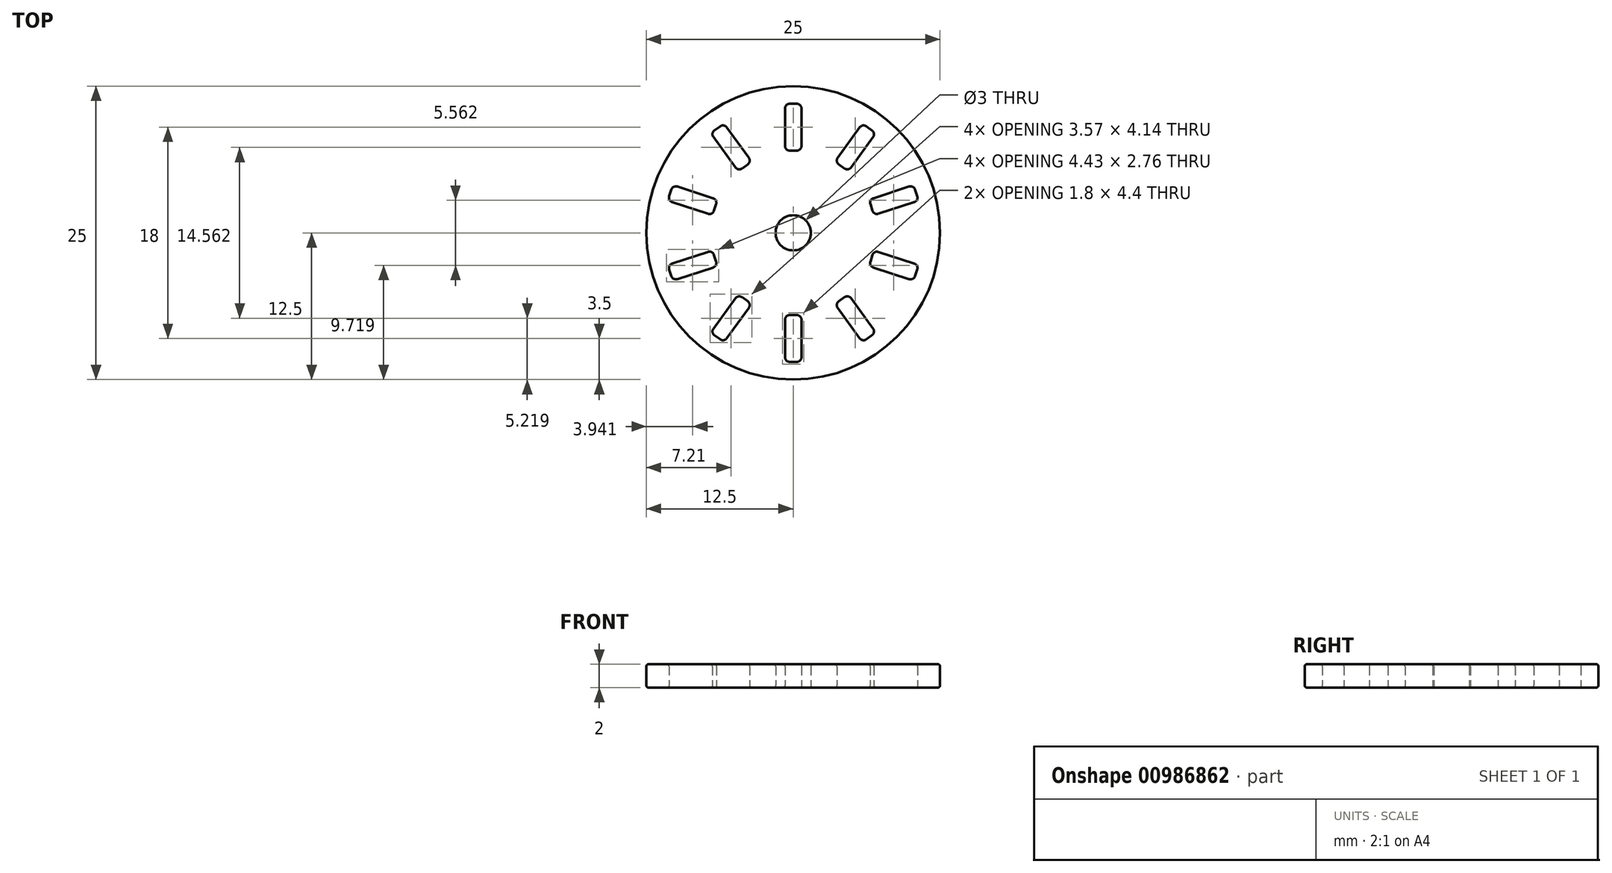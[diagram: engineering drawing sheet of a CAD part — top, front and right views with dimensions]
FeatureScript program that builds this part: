
annotation { "Feature Type Name" : "Feature", "Feature Type Description" : "" }
export const myFeature = defineFeature(function(context is Context, id is Id, definition is map)
    precondition{}
    {
        {
            var Q0;
            Q0=qCreatedBy(makeId("Top.planeOp"),FACE);
            var sketch = newSketch(context, id + "F0", { "sketchPlane" : qUnion([Q0])});
            skCircle(sketch, "E0", {"center": v(0, 0) * mm, "radius": 12.5 * mm});
            skCircle(sketch, "E1", {"center": v(0, 0) * mm, "radius": 9 * mm, "construction": true});
            skLineSegment(sketch, "E2.bottom", {"start": v(0.3, 11) * mm, "end": v(-0.3, 11) * mm});
            skLineSegment(sketch, "E2.top", {"start": v(0.3, 7) * mm, "end": v(-0.3, 7) * mm});
            skLineSegment(sketch, "E2.left", {"start": v(0.7, 10.6) * mm, "end": v(0.7, 7.4) * mm});
            skLineSegment(sketch, "E2.right", {"start": v(-0.7, 10.6) * mm, "end": v(-0.7, 7.4) * mm});
            skPoint(sketch, "E2.middle", {"position": v(0, 9) * mm});
            skPoint(sketch, "E3.visualSharp", {"position": v(-0.7, 11) * mm});
            skArc(sketch, "E3.filletArc", {"start": v(-0.3, 11) * mm, "mid": v(-0.58, 10.88) * mm, "end": v(-0.7, 10.6) * mm});
            skPoint(sketch, "E4.visualSharp", {"position": v(0.7, 11) * mm});
            skArc(sketch, "E4.filletArc", {"start": v(0.7, 10.6) * mm, "mid": v(0.58, 10.88) * mm, "end": v(0.3, 11) * mm});
            skPoint(sketch, "E5.visualSharp", {"position": v(0.7, 7) * mm});
            skArc(sketch, "E5.filletArc", {"start": v(0.3, 7) * mm, "mid": v(0.58, 7.12) * mm, "end": v(0.7, 7.4) * mm});
            skPoint(sketch, "E6.visualSharp", {"position": v(-0.7, 7) * mm});
            skArc(sketch, "E6.filletArc", {"start": v(-0.7, 7.4) * mm, "mid": v(-0.58, 7.12) * mm, "end": v(-0.3, 7) * mm});
            skLineSegment(sketch, "E7.1.0", {"start": v(-5.66, 8.99) * mm, "end": v(-3.78, 6.4) * mm});
            skPoint(sketch, "E7.1.1", {"position": v(-3.55, 6.07) * mm});
            skPoint(sketch, "E7.1.2", {"position": v(-5.3, 7.28) * mm});
            skPoint(sketch, "E7.1.3", {"position": v(-4.68, 5.25) * mm});
            skLineSegment(sketch, "E7.1.4", {"start": v(-6.8, 8.16) * mm, "end": v(-4.92, 5.58) * mm});
            skLineSegment(sketch, "E7.1.5", {"start": v(-3.87, 5.84) * mm, "end": v(-4.36, 5.49) * mm});
            skLineSegment(sketch, "E7.1.6", {"start": v(-6.22, 9.08) * mm, "end": v(-6.7, 8.72) * mm});
            skPoint(sketch, "E7.1.7", {"position": v(-7.03, 8.49) * mm});
            skPoint(sketch, "E7.1.8", {"position": v(-5.9, 9.31) * mm});
            skArc(sketch, "E7.1.9", {"start": v(-3.87, 5.84) * mm, "mid": v(-3.71, 6.1) * mm, "end": v(-3.78, 6.4) * mm});
            skArc(sketch, "E7.1.10", {"start": v(-6.7, 8.72) * mm, "mid": v(-6.87, 8.46) * mm, "end": v(-6.8, 8.16) * mm});
            skArc(sketch, "E7.1.11", {"start": v(-4.92, 5.58) * mm, "mid": v(-4.65, 5.42) * mm, "end": v(-4.36, 5.49) * mm});
            skArc(sketch, "E7.1.12", {"start": v(-5.66, 8.99) * mm, "mid": v(-5.93, 9.15) * mm, "end": v(-6.22, 9.08) * mm});
            skLineSegment(sketch, "E7.2.0", {"start": v(-9.86, 3.94) * mm, "end": v(-6.82, 2.95) * mm});
            skPoint(sketch, "E7.2.1", {"position": v(-6.44, 2.83) * mm});
            skPoint(sketch, "E7.2.2", {"position": v(-8.56, 2.78) * mm});
            skPoint(sketch, "E7.2.3", {"position": v(-6.87, 1.5) * mm});
            skLineSegment(sketch, "E7.2.4", {"start": v(-10.3, 2.6) * mm, "end": v(-7.25, 1.62) * mm});
            skLineSegment(sketch, "E7.2.5", {"start": v(-6.56, 2.45) * mm, "end": v(-6.75, 1.88) * mm});
            skLineSegment(sketch, "E7.2.6", {"start": v(-10.37, 3.68) * mm, "end": v(-10.55, 3.11) * mm});
            skPoint(sketch, "E7.2.7", {"position": v(-10.68, 2.73) * mm});
            skPoint(sketch, "E7.2.8", {"position": v(-10.25, 4.06) * mm});
            skArc(sketch, "E7.2.9", {"start": v(-6.56, 2.45) * mm, "mid": v(-6.59, 2.75) * mm, "end": v(-6.82, 2.95) * mm});
            skArc(sketch, "E7.2.10", {"start": v(-10.55, 3.11) * mm, "mid": v(-10.53, 2.8) * mm, "end": v(-10.3, 2.6) * mm});
            skArc(sketch, "E7.2.11", {"start": v(-7.25, 1.62) * mm, "mid": v(-6.95, 1.65) * mm, "end": v(-6.75, 1.88) * mm});
            skArc(sketch, "E7.2.12", {"start": v(-9.86, 3.94) * mm, "mid": v(-10.17, 3.92) * mm, "end": v(-10.37, 3.68) * mm});
            skLineSegment(sketch, "E7.3.0", {"start": v(-10.3, -2.6) * mm, "end": v(-7.25, -1.62) * mm});
            skPoint(sketch, "E7.3.1", {"position": v(-6.87, -1.5) * mm});
            skPoint(sketch, "E7.3.2", {"position": v(-8.56, -2.78) * mm});
            skPoint(sketch, "E7.3.3", {"position": v(-6.44, -2.83) * mm});
            skLineSegment(sketch, "E7.3.4", {"start": v(-9.86, -3.94) * mm, "end": v(-6.82, -2.95) * mm});
            skLineSegment(sketch, "E7.3.5", {"start": v(-6.75, -1.88) * mm, "end": v(-6.56, -2.45) * mm});
            skLineSegment(sketch, "E7.3.6", {"start": v(-10.55, -3.11) * mm, "end": v(-10.37, -3.68) * mm});
            skPoint(sketch, "E7.3.7", {"position": v(-10.25, -4.06) * mm});
            skPoint(sketch, "E7.3.8", {"position": v(-10.68, -2.73) * mm});
            skArc(sketch, "E7.3.9", {"start": v(-6.75, -1.88) * mm, "mid": v(-6.95, -1.65) * mm, "end": v(-7.25, -1.62) * mm});
            skArc(sketch, "E7.3.10", {"start": v(-10.37, -3.68) * mm, "mid": v(-10.17, -3.92) * mm, "end": v(-9.86, -3.94) * mm});
            skArc(sketch, "E7.3.11", {"start": v(-6.82, -2.95) * mm, "mid": v(-6.59, -2.75) * mm, "end": v(-6.56, -2.45) * mm});
            skArc(sketch, "E7.3.12", {"start": v(-10.3, -2.6) * mm, "mid": v(-10.53, -2.8) * mm, "end": v(-10.55, -3.11) * mm});
            skLineSegment(sketch, "E7.4.0", {"start": v(-6.8, -8.16) * mm, "end": v(-4.92, -5.58) * mm});
            skPoint(sketch, "E7.4.1", {"position": v(-4.68, -5.25) * mm});
            skPoint(sketch, "E7.4.2", {"position": v(-5.3, -7.28) * mm});
            skPoint(sketch, "E7.4.3", {"position": v(-3.55, -6.07) * mm});
            skLineSegment(sketch, "E7.4.4", {"start": v(-5.66, -8.99) * mm, "end": v(-3.78, -6.4) * mm});
            skLineSegment(sketch, "E7.4.5", {"start": v(-4.36, -5.49) * mm, "end": v(-3.87, -5.84) * mm});
            skLineSegment(sketch, "E7.4.6", {"start": v(-6.7, -8.72) * mm, "end": v(-6.22, -9.08) * mm});
            skPoint(sketch, "E7.4.7", {"position": v(-5.9, -9.31) * mm});
            skPoint(sketch, "E7.4.8", {"position": v(-7.03, -8.49) * mm});
            skArc(sketch, "E7.4.9", {"start": v(-4.36, -5.49) * mm, "mid": v(-4.65, -5.42) * mm, "end": v(-4.92, -5.58) * mm});
            skArc(sketch, "E7.4.10", {"start": v(-6.22, -9.08) * mm, "mid": v(-5.93, -9.15) * mm, "end": v(-5.66, -8.99) * mm});
            skArc(sketch, "E7.4.11", {"start": v(-3.78, -6.4) * mm, "mid": v(-3.71, -6.1) * mm, "end": v(-3.87, -5.84) * mm});
            skArc(sketch, "E7.4.12", {"start": v(-6.8, -8.16) * mm, "mid": v(-6.87, -8.46) * mm, "end": v(-6.7, -8.72) * mm});
            skLineSegment(sketch, "E7.5.0", {"start": v(-0.7, -10.6) * mm, "end": v(-0.7, -7.4) * mm});
            skPoint(sketch, "E7.5.1", {"position": v(-0.7, -7) * mm});
            skPoint(sketch, "E7.5.2", {"position": v(0, -9) * mm});
            skPoint(sketch, "E7.5.3", {"position": v(0.7, -7) * mm});
            skLineSegment(sketch, "E7.5.4", {"start": v(0.7, -10.6) * mm, "end": v(0.7, -7.4) * mm});
            skLineSegment(sketch, "E7.5.5", {"start": v(-0.3, -7) * mm, "end": v(0.3, -7) * mm});
            skLineSegment(sketch, "E7.5.6", {"start": v(-0.3, -11) * mm, "end": v(0.3, -11) * mm});
            skPoint(sketch, "E7.5.7", {"position": v(0.7, -11) * mm});
            skPoint(sketch, "E7.5.8", {"position": v(-0.7, -11) * mm});
            skArc(sketch, "E7.5.9", {"start": v(-0.3, -7) * mm, "mid": v(-0.58, -7.12) * mm, "end": v(-0.7, -7.4) * mm});
            skArc(sketch, "E7.5.10", {"start": v(0.3, -11) * mm, "mid": v(0.58, -10.88) * mm, "end": v(0.7, -10.6) * mm});
            skArc(sketch, "E7.5.11", {"start": v(0.7, -7.4) * mm, "mid": v(0.58, -7.12) * mm, "end": v(0.3, -7) * mm});
            skArc(sketch, "E7.5.12", {"start": v(-0.7, -10.6) * mm, "mid": v(-0.58, -10.88) * mm, "end": v(-0.3, -11) * mm});
            skLineSegment(sketch, "E7.6.0", {"start": v(5.66, -8.99) * mm, "end": v(3.78, -6.4) * mm});
            skPoint(sketch, "E7.6.1", {"position": v(3.55, -6.07) * mm});
            skPoint(sketch, "E7.6.2", {"position": v(5.3, -7.28) * mm});
            skPoint(sketch, "E7.6.3", {"position": v(4.68, -5.25) * mm});
            skLineSegment(sketch, "E7.6.4", {"start": v(6.8, -8.16) * mm, "end": v(4.92, -5.58) * mm});
            skLineSegment(sketch, "E7.6.5", {"start": v(3.87, -5.84) * mm, "end": v(4.36, -5.49) * mm});
            skLineSegment(sketch, "E7.6.6", {"start": v(6.22, -9.08) * mm, "end": v(6.7, -8.72) * mm});
            skPoint(sketch, "E7.6.7", {"position": v(7.03, -8.49) * mm});
            skPoint(sketch, "E7.6.8", {"position": v(5.9, -9.31) * mm});
            skArc(sketch, "E7.6.9", {"start": v(3.87, -5.84) * mm, "mid": v(3.71, -6.1) * mm, "end": v(3.78, -6.4) * mm});
            skArc(sketch, "E7.6.10", {"start": v(6.7, -8.72) * mm, "mid": v(6.87, -8.46) * mm, "end": v(6.8, -8.16) * mm});
            skArc(sketch, "E7.6.11", {"start": v(4.92, -5.58) * mm, "mid": v(4.65, -5.42) * mm, "end": v(4.36, -5.49) * mm});
            skArc(sketch, "E7.6.12", {"start": v(5.66, -8.99) * mm, "mid": v(5.93, -9.15) * mm, "end": v(6.22, -9.08) * mm});
            skLineSegment(sketch, "E7.7.0", {"start": v(9.86, -3.94) * mm, "end": v(6.82, -2.95) * mm});
            skPoint(sketch, "E7.7.1", {"position": v(6.44, -2.83) * mm});
            skPoint(sketch, "E7.7.2", {"position": v(8.56, -2.78) * mm});
            skPoint(sketch, "E7.7.3", {"position": v(6.87, -1.5) * mm});
            skLineSegment(sketch, "E7.7.4", {"start": v(10.3, -2.6) * mm, "end": v(7.25, -1.62) * mm});
            skLineSegment(sketch, "E7.7.5", {"start": v(6.56, -2.45) * mm, "end": v(6.75, -1.88) * mm});
            skLineSegment(sketch, "E7.7.6", {"start": v(10.37, -3.68) * mm, "end": v(10.55, -3.11) * mm});
            skPoint(sketch, "E7.7.7", {"position": v(10.68, -2.73) * mm});
            skPoint(sketch, "E7.7.8", {"position": v(10.25, -4.06) * mm});
            skArc(sketch, "E7.7.9", {"start": v(6.56, -2.45) * mm, "mid": v(6.59, -2.75) * mm, "end": v(6.82, -2.95) * mm});
            skArc(sketch, "E7.7.10", {"start": v(10.55, -3.11) * mm, "mid": v(10.53, -2.8) * mm, "end": v(10.3, -2.6) * mm});
            skArc(sketch, "E7.7.11", {"start": v(7.25, -1.62) * mm, "mid": v(6.95, -1.65) * mm, "end": v(6.75, -1.88) * mm});
            skArc(sketch, "E7.7.12", {"start": v(9.86, -3.94) * mm, "mid": v(10.17, -3.92) * mm, "end": v(10.37, -3.68) * mm});
            skLineSegment(sketch, "E7.8.0", {"start": v(10.3, 2.6) * mm, "end": v(7.25, 1.62) * mm});
            skPoint(sketch, "E7.8.1", {"position": v(6.87, 1.5) * mm});
            skPoint(sketch, "E7.8.2", {"position": v(8.56, 2.78) * mm});
            skPoint(sketch, "E7.8.3", {"position": v(6.44, 2.83) * mm});
            skLineSegment(sketch, "E7.8.4", {"start": v(9.86, 3.94) * mm, "end": v(6.82, 2.95) * mm});
            skLineSegment(sketch, "E7.8.5", {"start": v(6.75, 1.88) * mm, "end": v(6.56, 2.45) * mm});
            skLineSegment(sketch, "E7.8.6", {"start": v(10.55, 3.11) * mm, "end": v(10.37, 3.68) * mm});
            skPoint(sketch, "E7.8.7", {"position": v(10.25, 4.06) * mm});
            skPoint(sketch, "E7.8.8", {"position": v(10.68, 2.73) * mm});
            skArc(sketch, "E7.8.9", {"start": v(6.75, 1.88) * mm, "mid": v(6.95, 1.65) * mm, "end": v(7.25, 1.62) * mm});
            skArc(sketch, "E7.8.10", {"start": v(10.37, 3.68) * mm, "mid": v(10.17, 3.92) * mm, "end": v(9.86, 3.94) * mm});
            skArc(sketch, "E7.8.11", {"start": v(6.82, 2.95) * mm, "mid": v(6.59, 2.75) * mm, "end": v(6.56, 2.45) * mm});
            skArc(sketch, "E7.8.12", {"start": v(10.3, 2.6) * mm, "mid": v(10.53, 2.8) * mm, "end": v(10.55, 3.11) * mm});
            skLineSegment(sketch, "E7.9.0", {"start": v(6.8, 8.16) * mm, "end": v(4.92, 5.58) * mm});
            skPoint(sketch, "E7.9.1", {"position": v(4.68, 5.25) * mm});
            skPoint(sketch, "E7.9.2", {"position": v(5.3, 7.28) * mm});
            skPoint(sketch, "E7.9.3", {"position": v(3.55, 6.07) * mm});
            skLineSegment(sketch, "E7.9.4", {"start": v(5.66, 8.99) * mm, "end": v(3.78, 6.4) * mm});
            skLineSegment(sketch, "E7.9.5", {"start": v(4.36, 5.49) * mm, "end": v(3.87, 5.84) * mm});
            skLineSegment(sketch, "E7.9.6", {"start": v(6.7, 8.72) * mm, "end": v(6.22, 9.08) * mm});
            skPoint(sketch, "E7.9.7", {"position": v(5.9, 9.31) * mm});
            skPoint(sketch, "E7.9.8", {"position": v(7.03, 8.49) * mm});
            skArc(sketch, "E7.9.9", {"start": v(4.36, 5.49) * mm, "mid": v(4.65, 5.42) * mm, "end": v(4.92, 5.58) * mm});
            skArc(sketch, "E7.9.10", {"start": v(6.22, 9.08) * mm, "mid": v(5.93, 9.15) * mm, "end": v(5.66, 8.99) * mm});
            skArc(sketch, "E7.9.11", {"start": v(3.78, 6.4) * mm, "mid": v(3.71, 6.1) * mm, "end": v(3.87, 5.84) * mm});
            skArc(sketch, "E7.9.12", {"start": v(6.8, 8.16) * mm, "mid": v(6.87, 8.46) * mm, "end": v(6.7, 8.72) * mm});
            skCircle(sketch, "E8", {"center": v(0, 0) * mm, "radius": 1.5 * mm});
            skSolve(sketch);
        }
        {
            var Q0;
            Q0=makeQuery(id+"F0.imprint","IMPRINT",FACE,{"disambiguationData":[TD([[makeQuery(id+"F0.imprint","IMPRINT",EDGE,{"derivedFrom":sQuery(id+"F0.wireOp",EDGE,"E0")}),1.0]])]});
            extrude(context, id + "F1", {"entities" : qUnion([Q0]), "depth" : 2 * mm, "offsetDistance" : 25 * mm});
        }
        {
            var Q0;
            Q0=makeQuery(id+"F1.opExtrude","CAP_FACE",FACE,{"disambiguationData":[OSD([sQuery(id+"F0.wireOp",EDGE,"E0"),sQuery(id+"F0.wireOp",EDGE,"E2.bottom"),sQuery(id+"F0.wireOp",EDGE,"E2.top"),sQuery(id+"F0.wireOp",EDGE,"E2.left"),sQuery(id+"F0.wireOp",EDGE,"E2.right"),sQuery(id+"F0.wireOp",EDGE,"E3.filletArc"),sQuery(id+"F0.wireOp",EDGE,"E4.filletArc"),sQuery(id+"F0.wireOp",EDGE,"E5.filletArc"),sQuery(id+"F0.wireOp",EDGE,"E6.filletArc"),sQuery(id+"F0.wireOp",EDGE,"E7.1.0"),sQuery(id+"F0.wireOp",EDGE,"E7.1.4"),sQuery(id+"F0.wireOp",EDGE,"E7.1.5"),sQuery(id+"F0.wireOp",EDGE,"E7.1.6"),sQuery(id+"F0.wireOp",EDGE,"E7.1.9"),sQuery(id+"F0.wireOp",EDGE,"E7.1.10"),sQuery(id+"F0.wireOp",EDGE,"E7.1.11"),sQuery(id+"F0.wireOp",EDGE,"E7.1.12"),sQuery(id+"F0.wireOp",EDGE,"E7.2.0"),sQuery(id+"F0.wireOp",EDGE,"E7.2.4"),sQuery(id+"F0.wireOp",EDGE,"E7.2.5"),sQuery(id+"F0.wireOp",EDGE,"E7.2.6"),sQuery(id+"F0.wireOp",EDGE,"E7.2.9"),sQuery(id+"F0.wireOp",EDGE,"E7.2.10"),sQuery(id+"F0.wireOp",EDGE,"E7.2.11"),sQuery(id+"F0.wireOp",EDGE,"E7.2.12"),sQuery(id+"F0.wireOp",EDGE,"E7.3.0"),sQuery(id+"F0.wireOp",EDGE,"E7.3.4"),sQuery(id+"F0.wireOp",EDGE,"E7.3.5"),sQuery(id+"F0.wireOp",EDGE,"E7.3.6"),sQuery(id+"F0.wireOp",EDGE,"E7.3.9"),sQuery(id+"F0.wireOp",EDGE,"E7.3.10"),sQuery(id+"F0.wireOp",EDGE,"E7.3.11"),sQuery(id+"F0.wireOp",EDGE,"E7.3.12"),sQuery(id+"F0.wireOp",EDGE,"E7.4.0"),sQuery(id+"F0.wireOp",EDGE,"E7.4.4"),sQuery(id+"F0.wireOp",EDGE,"E7.4.5"),sQuery(id+"F0.wireOp",EDGE,"E7.4.6"),sQuery(id+"F0.wireOp",EDGE,"E7.4.9"),sQuery(id+"F0.wireOp",EDGE,"E7.4.10"),sQuery(id+"F0.wireOp",EDGE,"E7.4.11"),sQuery(id+"F0.wireOp",EDGE,"E7.4.12"),sQuery(id+"F0.wireOp",EDGE,"E7.5.0"),sQuery(id+"F0.wireOp",EDGE,"E7.5.4"),sQuery(id+"F0.wireOp",EDGE,"E7.5.5"),sQuery(id+"F0.wireOp",EDGE,"E7.5.6"),sQuery(id+"F0.wireOp",EDGE,"E7.5.9"),sQuery(id+"F0.wireOp",EDGE,"E7.5.10"),sQuery(id+"F0.wireOp",EDGE,"E7.5.11"),sQuery(id+"F0.wireOp",EDGE,"E7.5.12"),sQuery(id+"F0.wireOp",EDGE,"E7.6.0"),sQuery(id+"F0.wireOp",EDGE,"E7.6.4"),sQuery(id+"F0.wireOp",EDGE,"E7.6.5"),sQuery(id+"F0.wireOp",EDGE,"E7.6.6"),sQuery(id+"F0.wireOp",EDGE,"E7.6.9"),sQuery(id+"F0.wireOp",EDGE,"E7.6.10"),sQuery(id+"F0.wireOp",EDGE,"E7.6.11"),sQuery(id+"F0.wireOp",EDGE,"E7.6.12"),sQuery(id+"F0.wireOp",EDGE,"E7.7.0"),sQuery(id+"F0.wireOp",EDGE,"E7.7.4"),sQuery(id+"F0.wireOp",EDGE,"E7.7.5"),sQuery(id+"F0.wireOp",EDGE,"E7.7.6"),sQuery(id+"F0.wireOp",EDGE,"E7.7.9"),sQuery(id+"F0.wireOp",EDGE,"E7.7.10"),sQuery(id+"F0.wireOp",EDGE,"E7.7.11"),sQuery(id+"F0.wireOp",EDGE,"E7.7.12"),sQuery(id+"F0.wireOp",EDGE,"E7.8.0"),sQuery(id+"F0.wireOp",EDGE,"E7.8.4"),sQuery(id+"F0.wireOp",EDGE,"E7.8.5"),sQuery(id+"F0.wireOp",EDGE,"E7.8.6"),sQuery(id+"F0.wireOp",EDGE,"E7.8.9"),sQuery(id+"F0.wireOp",EDGE,"E7.8.10"),sQuery(id+"F0.wireOp",EDGE,"E7.8.11"),sQuery(id+"F0.wireOp",EDGE,"E7.8.12"),sQuery(id+"F0.wireOp",EDGE,"E7.9.0"),sQuery(id+"F0.wireOp",EDGE,"E7.9.4"),sQuery(id+"F0.wireOp",EDGE,"E7.9.5"),sQuery(id+"F0.wireOp",EDGE,"E7.9.6"),sQuery(id+"F0.wireOp",EDGE,"E7.9.9"),sQuery(id+"F0.wireOp",EDGE,"E7.9.10"),sQuery(id+"F0.wireOp",EDGE,"E7.9.11"),sQuery(id+"F0.wireOp",EDGE,"E7.9.12"),sQuery(id+"F0.wireOp",EDGE,"E7.10.0"),sQuery(id+"F0.wireOp",EDGE,"E7.10.4"),sQuery(id+"F0.wireOp",EDGE,"E7.10.5"),sQuery(id+"F0.wireOp",EDGE,"E7.10.6"),sQuery(id+"F0.wireOp",EDGE,"E7.10.9"),sQuery(id+"F0.wireOp",EDGE,"E7.10.10"),sQuery(id+"F0.wireOp",EDGE,"E7.10.11"),sQuery(id+"F0.wireOp",EDGE,"E7.10.12"),sQuery(id+"F0.wireOp",EDGE,"E7.11.0"),sQuery(id+"F0.wireOp",EDGE,"E7.11.4"),sQuery(id+"F0.wireOp",EDGE,"E7.11.5"),sQuery(id+"F0.wireOp",EDGE,"E7.11.6"),sQuery(id+"F0.wireOp",EDGE,"E7.11.9"),sQuery(id+"F0.wireOp",EDGE,"E7.11.10"),sQuery(id+"F0.wireOp",EDGE,"E7.11.11"),sQuery(id+"F0.wireOp",EDGE,"E7.11.12"),sQuery(id+"F0.wireOp",EDGE,"E7.12.0"),sQuery(id+"F0.wireOp",EDGE,"E7.12.4"),sQuery(id+"F0.wireOp",EDGE,"E7.12.5"),sQuery(id+"F0.wireOp",EDGE,"E7.12.6"),sQuery(id+"F0.wireOp",EDGE,"E7.12.9"),sQuery(id+"F0.wireOp",EDGE,"E7.12.10"),sQuery(id+"F0.wireOp",EDGE,"E7.12.11"),sQuery(id+"F0.wireOp",EDGE,"E7.12.12"),sQuery(id+"F0.wireOp",EDGE,"E7.13.0"),sQuery(id+"F0.wireOp",EDGE,"E7.13.4"),sQuery(id+"F0.wireOp",EDGE,"E7.13.5"),sQuery(id+"F0.wireOp",EDGE,"E7.13.6"),sQuery(id+"F0.wireOp",EDGE,"E7.13.9"),sQuery(id+"F0.wireOp",EDGE,"E7.13.10"),sQuery(id+"F0.wireOp",EDGE,"E7.13.11"),sQuery(id+"F0.wireOp",EDGE,"E7.13.12"),sQuery(id+"F0.wireOp",EDGE,"E7.14.0"),sQuery(id+"F0.wireOp",EDGE,"E7.14.4"),sQuery(id+"F0.wireOp",EDGE,"E7.14.5"),sQuery(id+"F0.wireOp",EDGE,"E7.14.6"),sQuery(id+"F0.wireOp",EDGE,"E7.14.9"),sQuery(id+"F0.wireOp",EDGE,"E7.14.10"),sQuery(id+"F0.wireOp",EDGE,"E7.14.11"),sQuery(id+"F0.wireOp",EDGE,"E7.14.12"),sQuery(id+"F0.wireOp",EDGE,"E7.15.0"),sQuery(id+"F0.wireOp",EDGE,"E7.15.4"),sQuery(id+"F0.wireOp",EDGE,"E7.15.5"),sQuery(id+"F0.wireOp",EDGE,"E7.15.6"),sQuery(id+"F0.wireOp",EDGE,"E7.15.9"),sQuery(id+"F0.wireOp",EDGE,"E7.15.10"),sQuery(id+"F0.wireOp",EDGE,"E7.15.11"),sQuery(id+"F0.wireOp",EDGE,"E7.15.12"),sQuery(id+"F0.wireOp",EDGE,"E7.16.0"),sQuery(id+"F0.wireOp",EDGE,"E7.16.4"),sQuery(id+"F0.wireOp",EDGE,"E7.16.5"),sQuery(id+"F0.wireOp",EDGE,"E7.16.6"),sQuery(id+"F0.wireOp",EDGE,"E7.16.9"),sQuery(id+"F0.wireOp",EDGE,"E7.16.10"),sQuery(id+"F0.wireOp",EDGE,"E7.16.11"),sQuery(id+"F0.wireOp",EDGE,"E7.16.12"),sQuery(id+"F0.wireOp",EDGE,"E7.17.0"),sQuery(id+"F0.wireOp",EDGE,"E7.17.4"),sQuery(id+"F0.wireOp",EDGE,"E7.17.5"),sQuery(id+"F0.wireOp",EDGE,"E7.17.6"),sQuery(id+"F0.wireOp",EDGE,"E7.17.9"),sQuery(id+"F0.wireOp",EDGE,"E7.17.10"),sQuery(id+"F0.wireOp",EDGE,"E7.17.11"),sQuery(id+"F0.wireOp",EDGE,"E7.17.12"),sQuery(id+"F0.wireOp",EDGE,"E7.18.0"),sQuery(id+"F0.wireOp",EDGE,"E7.18.4"),sQuery(id+"F0.wireOp",EDGE,"E7.18.5"),sQuery(id+"F0.wireOp",EDGE,"E7.18.6"),sQuery(id+"F0.wireOp",EDGE,"E7.18.9"),sQuery(id+"F0.wireOp",EDGE,"E7.18.10"),sQuery(id+"F0.wireOp",EDGE,"E7.18.11"),sQuery(id+"F0.wireOp",EDGE,"E7.18.12"),sQuery(id+"F0.wireOp",EDGE,"E7.19.0"),sQuery(id+"F0.wireOp",EDGE,"E7.19.4"),sQuery(id+"F0.wireOp",EDGE,"E7.19.5"),sQuery(id+"F0.wireOp",EDGE,"E7.19.6"),sQuery(id+"F0.wireOp",EDGE,"E7.19.9"),sQuery(id+"F0.wireOp",EDGE,"E7.19.10"),sQuery(id+"F0.wireOp",EDGE,"E7.19.11"),sQuery(id+"F0.wireOp",EDGE,"E7.19.12")])],"isStart":false});
            var Q1;
            Q1=makeQuery(id+"F1.opExtrude","CAP_FACE",FACE,{"disambiguationData":[OSD([sQuery(id+"F0.wireOp",EDGE,"E0"),sQuery(id+"F0.wireOp",EDGE,"E2.bottom"),sQuery(id+"F0.wireOp",EDGE,"E2.top"),sQuery(id+"F0.wireOp",EDGE,"E2.left"),sQuery(id+"F0.wireOp",EDGE,"E2.right"),sQuery(id+"F0.wireOp",EDGE,"E3.filletArc"),sQuery(id+"F0.wireOp",EDGE,"E4.filletArc"),sQuery(id+"F0.wireOp",EDGE,"E5.filletArc"),sQuery(id+"F0.wireOp",EDGE,"E6.filletArc"),sQuery(id+"F0.wireOp",EDGE,"E7.1.0"),sQuery(id+"F0.wireOp",EDGE,"E7.1.4"),sQuery(id+"F0.wireOp",EDGE,"E7.1.5"),sQuery(id+"F0.wireOp",EDGE,"E7.1.6"),sQuery(id+"F0.wireOp",EDGE,"E7.1.9"),sQuery(id+"F0.wireOp",EDGE,"E7.1.10"),sQuery(id+"F0.wireOp",EDGE,"E7.1.11"),sQuery(id+"F0.wireOp",EDGE,"E7.1.12"),sQuery(id+"F0.wireOp",EDGE,"E7.2.0"),sQuery(id+"F0.wireOp",EDGE,"E7.2.4"),sQuery(id+"F0.wireOp",EDGE,"E7.2.5"),sQuery(id+"F0.wireOp",EDGE,"E7.2.6"),sQuery(id+"F0.wireOp",EDGE,"E7.2.9"),sQuery(id+"F0.wireOp",EDGE,"E7.2.10"),sQuery(id+"F0.wireOp",EDGE,"E7.2.11"),sQuery(id+"F0.wireOp",EDGE,"E7.2.12"),sQuery(id+"F0.wireOp",EDGE,"E7.3.0"),sQuery(id+"F0.wireOp",EDGE,"E7.3.4"),sQuery(id+"F0.wireOp",EDGE,"E7.3.5"),sQuery(id+"F0.wireOp",EDGE,"E7.3.6"),sQuery(id+"F0.wireOp",EDGE,"E7.3.9"),sQuery(id+"F0.wireOp",EDGE,"E7.3.10"),sQuery(id+"F0.wireOp",EDGE,"E7.3.11"),sQuery(id+"F0.wireOp",EDGE,"E7.3.12"),sQuery(id+"F0.wireOp",EDGE,"E7.4.0"),sQuery(id+"F0.wireOp",EDGE,"E7.4.4"),sQuery(id+"F0.wireOp",EDGE,"E7.4.5"),sQuery(id+"F0.wireOp",EDGE,"E7.4.6"),sQuery(id+"F0.wireOp",EDGE,"E7.4.9"),sQuery(id+"F0.wireOp",EDGE,"E7.4.10"),sQuery(id+"F0.wireOp",EDGE,"E7.4.11"),sQuery(id+"F0.wireOp",EDGE,"E7.4.12"),sQuery(id+"F0.wireOp",EDGE,"E7.5.0"),sQuery(id+"F0.wireOp",EDGE,"E7.5.4"),sQuery(id+"F0.wireOp",EDGE,"E7.5.5"),sQuery(id+"F0.wireOp",EDGE,"E7.5.6"),sQuery(id+"F0.wireOp",EDGE,"E7.5.9"),sQuery(id+"F0.wireOp",EDGE,"E7.5.10"),sQuery(id+"F0.wireOp",EDGE,"E7.5.11"),sQuery(id+"F0.wireOp",EDGE,"E7.5.12"),sQuery(id+"F0.wireOp",EDGE,"E7.6.0"),sQuery(id+"F0.wireOp",EDGE,"E7.6.4"),sQuery(id+"F0.wireOp",EDGE,"E7.6.5"),sQuery(id+"F0.wireOp",EDGE,"E7.6.6"),sQuery(id+"F0.wireOp",EDGE,"E7.6.9"),sQuery(id+"F0.wireOp",EDGE,"E7.6.10"),sQuery(id+"F0.wireOp",EDGE,"E7.6.11"),sQuery(id+"F0.wireOp",EDGE,"E7.6.12"),sQuery(id+"F0.wireOp",EDGE,"E7.7.0"),sQuery(id+"F0.wireOp",EDGE,"E7.7.4"),sQuery(id+"F0.wireOp",EDGE,"E7.7.5"),sQuery(id+"F0.wireOp",EDGE,"E7.7.6"),sQuery(id+"F0.wireOp",EDGE,"E7.7.9"),sQuery(id+"F0.wireOp",EDGE,"E7.7.10"),sQuery(id+"F0.wireOp",EDGE,"E7.7.11"),sQuery(id+"F0.wireOp",EDGE,"E7.7.12"),sQuery(id+"F0.wireOp",EDGE,"E7.8.0"),sQuery(id+"F0.wireOp",EDGE,"E7.8.4"),sQuery(id+"F0.wireOp",EDGE,"E7.8.5"),sQuery(id+"F0.wireOp",EDGE,"E7.8.6"),sQuery(id+"F0.wireOp",EDGE,"E7.8.9"),sQuery(id+"F0.wireOp",EDGE,"E7.8.10"),sQuery(id+"F0.wireOp",EDGE,"E7.8.11"),sQuery(id+"F0.wireOp",EDGE,"E7.8.12"),sQuery(id+"F0.wireOp",EDGE,"E7.9.0"),sQuery(id+"F0.wireOp",EDGE,"E7.9.4"),sQuery(id+"F0.wireOp",EDGE,"E7.9.5"),sQuery(id+"F0.wireOp",EDGE,"E7.9.6"),sQuery(id+"F0.wireOp",EDGE,"E7.9.9"),sQuery(id+"F0.wireOp",EDGE,"E7.9.10"),sQuery(id+"F0.wireOp",EDGE,"E7.9.11"),sQuery(id+"F0.wireOp",EDGE,"E7.9.12"),sQuery(id+"F0.wireOp",EDGE,"E7.10.0"),sQuery(id+"F0.wireOp",EDGE,"E7.10.4"),sQuery(id+"F0.wireOp",EDGE,"E7.10.5"),sQuery(id+"F0.wireOp",EDGE,"E7.10.6"),sQuery(id+"F0.wireOp",EDGE,"E7.10.9"),sQuery(id+"F0.wireOp",EDGE,"E7.10.10"),sQuery(id+"F0.wireOp",EDGE,"E7.10.11"),sQuery(id+"F0.wireOp",EDGE,"E7.10.12"),sQuery(id+"F0.wireOp",EDGE,"E7.11.0"),sQuery(id+"F0.wireOp",EDGE,"E7.11.4"),sQuery(id+"F0.wireOp",EDGE,"E7.11.5"),sQuery(id+"F0.wireOp",EDGE,"E7.11.6"),sQuery(id+"F0.wireOp",EDGE,"E7.11.9"),sQuery(id+"F0.wireOp",EDGE,"E7.11.10"),sQuery(id+"F0.wireOp",EDGE,"E7.11.11"),sQuery(id+"F0.wireOp",EDGE,"E7.11.12"),sQuery(id+"F0.wireOp",EDGE,"E7.12.0"),sQuery(id+"F0.wireOp",EDGE,"E7.12.4"),sQuery(id+"F0.wireOp",EDGE,"E7.12.5"),sQuery(id+"F0.wireOp",EDGE,"E7.12.6"),sQuery(id+"F0.wireOp",EDGE,"E7.12.9"),sQuery(id+"F0.wireOp",EDGE,"E7.12.10"),sQuery(id+"F0.wireOp",EDGE,"E7.12.11"),sQuery(id+"F0.wireOp",EDGE,"E7.12.12"),sQuery(id+"F0.wireOp",EDGE,"E7.13.0"),sQuery(id+"F0.wireOp",EDGE,"E7.13.4"),sQuery(id+"F0.wireOp",EDGE,"E7.13.5"),sQuery(id+"F0.wireOp",EDGE,"E7.13.6"),sQuery(id+"F0.wireOp",EDGE,"E7.13.9"),sQuery(id+"F0.wireOp",EDGE,"E7.13.10"),sQuery(id+"F0.wireOp",EDGE,"E7.13.11"),sQuery(id+"F0.wireOp",EDGE,"E7.13.12"),sQuery(id+"F0.wireOp",EDGE,"E7.14.0"),sQuery(id+"F0.wireOp",EDGE,"E7.14.4"),sQuery(id+"F0.wireOp",EDGE,"E7.14.5"),sQuery(id+"F0.wireOp",EDGE,"E7.14.6"),sQuery(id+"F0.wireOp",EDGE,"E7.14.9"),sQuery(id+"F0.wireOp",EDGE,"E7.14.10"),sQuery(id+"F0.wireOp",EDGE,"E7.14.11"),sQuery(id+"F0.wireOp",EDGE,"E7.14.12"),sQuery(id+"F0.wireOp",EDGE,"E7.15.0"),sQuery(id+"F0.wireOp",EDGE,"E7.15.4"),sQuery(id+"F0.wireOp",EDGE,"E7.15.5"),sQuery(id+"F0.wireOp",EDGE,"E7.15.6"),sQuery(id+"F0.wireOp",EDGE,"E7.15.9"),sQuery(id+"F0.wireOp",EDGE,"E7.15.10"),sQuery(id+"F0.wireOp",EDGE,"E7.15.11"),sQuery(id+"F0.wireOp",EDGE,"E7.15.12"),sQuery(id+"F0.wireOp",EDGE,"E7.16.0"),sQuery(id+"F0.wireOp",EDGE,"E7.16.4"),sQuery(id+"F0.wireOp",EDGE,"E7.16.5"),sQuery(id+"F0.wireOp",EDGE,"E7.16.6"),sQuery(id+"F0.wireOp",EDGE,"E7.16.9"),sQuery(id+"F0.wireOp",EDGE,"E7.16.10"),sQuery(id+"F0.wireOp",EDGE,"E7.16.11"),sQuery(id+"F0.wireOp",EDGE,"E7.16.12"),sQuery(id+"F0.wireOp",EDGE,"E7.17.0"),sQuery(id+"F0.wireOp",EDGE,"E7.17.4"),sQuery(id+"F0.wireOp",EDGE,"E7.17.5"),sQuery(id+"F0.wireOp",EDGE,"E7.17.6"),sQuery(id+"F0.wireOp",EDGE,"E7.17.9"),sQuery(id+"F0.wireOp",EDGE,"E7.17.10"),sQuery(id+"F0.wireOp",EDGE,"E7.17.11"),sQuery(id+"F0.wireOp",EDGE,"E7.17.12"),sQuery(id+"F0.wireOp",EDGE,"E7.18.0"),sQuery(id+"F0.wireOp",EDGE,"E7.18.4"),sQuery(id+"F0.wireOp",EDGE,"E7.18.5"),sQuery(id+"F0.wireOp",EDGE,"E7.18.6"),sQuery(id+"F0.wireOp",EDGE,"E7.18.9"),sQuery(id+"F0.wireOp",EDGE,"E7.18.10"),sQuery(id+"F0.wireOp",EDGE,"E7.18.11"),sQuery(id+"F0.wireOp",EDGE,"E7.18.12"),sQuery(id+"F0.wireOp",EDGE,"E7.19.0"),sQuery(id+"F0.wireOp",EDGE,"E7.19.4"),sQuery(id+"F0.wireOp",EDGE,"E7.19.5"),sQuery(id+"F0.wireOp",EDGE,"E7.19.6"),sQuery(id+"F0.wireOp",EDGE,"E7.19.9"),sQuery(id+"F0.wireOp",EDGE,"E7.19.10"),sQuery(id+"F0.wireOp",EDGE,"E7.19.11"),sQuery(id+"F0.wireOp",EDGE,"E7.19.12")])],"isStart":true});
            fillet(context, id + "F2", {"entities" : qUnion([Q0, Q1]), "radius" : 0.2 * mm, "tangentPropagation" : true, "allowEdgeOverflow" : false});
        }
    });
